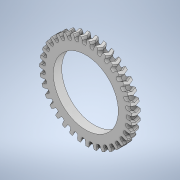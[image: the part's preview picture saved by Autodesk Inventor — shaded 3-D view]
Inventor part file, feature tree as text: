
AUTODESK INVENTOR PART (.ipt)
format: ipt  version: 2022 (Build 260153070, 153G)  size: 1,413,120 bytes
history: native  units: mm
features: sketch x2, extrude x2, helix x1, pattern_circular x1, mirror x1
ambient origin geometry x8: Origin, YZ Plane, XZ Plane, XY Plane, X Axis, Y Axis, Z Axis, Center Point
bodies: Solid1 (feature_tree)
feature tree (7):
  sketch  "Sketch1"  dims[d0=1.5mm d1=0.0mm]
  extrude  "Extrusion1"  TaperAngle=0.0deg  [1 undecoded]
  helix  "Coil1"  [1 undecoded]
  pattern_circular  "Circular Pattern1"  [2 undecoded]
  mirror  "Mirror1"
  extrude  "Extrusion2"  Depth=10.0mm TaperAngle=0.0deg
  sketch  "Sketch3"  dims[d2=273.26323mm d3=1.5mm d4=10.0mm d5=0.0mm d6=90.0deg d7=90.0deg d8=0.0mm d9=0.0mm d10=350.0mm d11=360.0deg d13=23.05mm d14=10.0mm d15=0.0mm]
note: 4 required parameter values undecoded (feature->parameter linkage not recoverable at this tier; creation-order binding heuristic only, values carry confidence <= 0.55)
